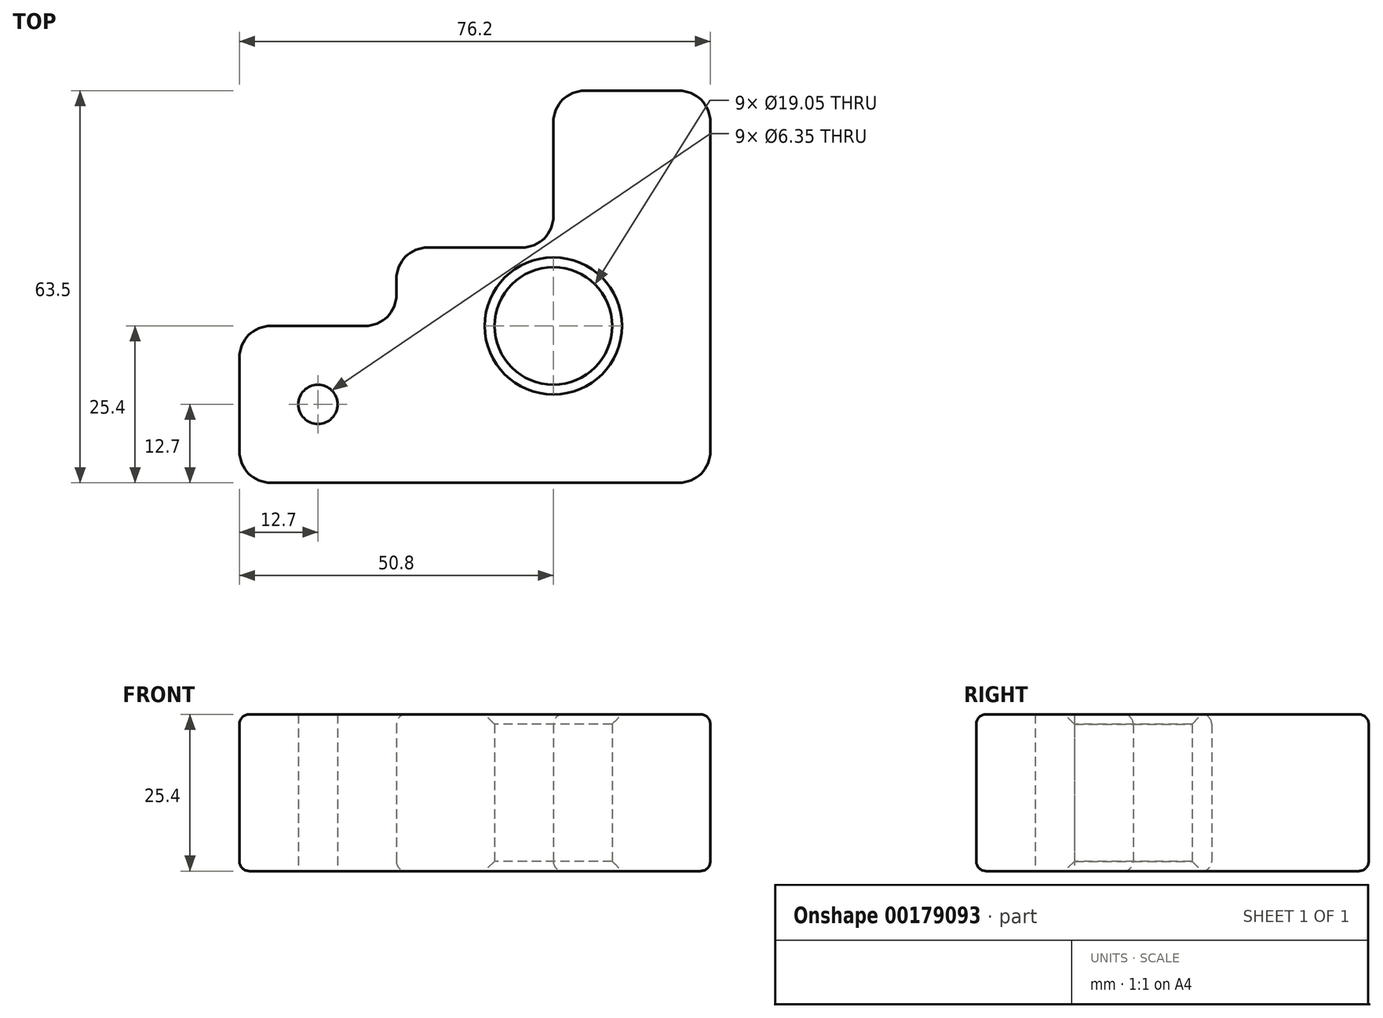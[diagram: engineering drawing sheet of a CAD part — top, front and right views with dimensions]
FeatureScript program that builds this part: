
annotation { "Feature Type Name" : "Feature", "Feature Type Description" : "" }
export const myFeature = defineFeature(function(context is Context, id is Id, definition is map)
    precondition{}
    {
        {
            var Q0;
            Q0=qCreatedBy(makeId("Top.planeOp"),FACE);
            var sketch = newSketch(context, id + "F0", { "sketchPlane" : qUnion([Q0])});
            skLineSegment(sketch, "E0", {"start": v(-25.4, 0) * mm, "end": v(0, 0) * mm});
            skLineSegment(sketch, "E1", {"start": v(0, 0) * mm, "end": v(0, 12.7) * mm});
            skLineSegment(sketch, "E2", {"start": v(0, 12.7) * mm, "end": v(25.4, 12.7) * mm});
            skLineSegment(sketch, "E3", {"start": v(25.4, 12.7) * mm, "end": v(25.4, 38.1) * mm});
            skLineSegment(sketch, "E4", {"start": v(25.4, 38.1) * mm, "end": v(50.8, 38.1) * mm});
            skLineSegment(sketch, "E5", {"start": v(50.8, 38.1) * mm, "end": v(50.8, -25.4) * mm});
            skLineSegment(sketch, "E6", {"start": v(50.8, -25.4) * mm, "end": v(-25.4, -25.4) * mm});
            skLineSegment(sketch, "E7", {"start": v(-25.4, -25.4) * mm, "end": v(-25.4, 0) * mm});
            skPoint(sketch, "E8", {"position": v(0, 0) * mm});
            skCircle(sketch, "E9", {"center": v(25.4, 0) * mm, "radius": 9.53 * mm});
            skCircle(sketch, "E10", {"center": v(-12.7, -12.7) * mm, "radius": 3.18 * mm});
            skSolve(sketch);
        }
        {
            var Q0;
            Q0=makeQuery(id+"F0.imprint","IMPRINT",FACE,{"disambiguationData":[TD([[makeQuery(id+"F0.imprint","IMPRINT",EDGE,{"derivedFrom":sQuery(id+"F0.wireOp",EDGE,"E0")}),-1.0]])]});
            extrude(context, id + "F1", {"entities" : qUnion([Q0]), "depth" : 25.4 * mm});
        }
        {
            var Q0;
            Q0=makeQuery(id+"F1.opExtrude","SWEPT_EDGE",EDGE,{"disambiguationData":[OSD([sQuery(id+"F0.wireOp",EDGE,"E4"),sQuery(id+"F0.wireOp",EDGE,"E5")])]});
            var Q1;
            Q1=makeQuery(id+"F1.opExtrude","SWEPT_EDGE",EDGE,{"disambiguationData":[OSD([sQuery(id+"F0.wireOp",EDGE,"E3"),sQuery(id+"F0.wireOp",EDGE,"E4")])]});
            var Q2;
            Q2=makeQuery(id+"F1.opExtrude","SWEPT_EDGE",EDGE,{"disambiguationData":[OSD([sQuery(id+"F0.wireOp",EDGE,"E2"),sQuery(id+"F0.wireOp",EDGE,"E3")])]});
            var Q3;
            Q3=makeQuery(id+"F1.opExtrude","SWEPT_EDGE",EDGE,{"disambiguationData":[OSD([sQuery(id+"F0.wireOp",EDGE,"E1"),sQuery(id+"F0.wireOp",EDGE,"E2")])]});
            var Q4;
            Q4=makeQuery(id+"F1.opExtrude","SWEPT_EDGE",EDGE,{"disambiguationData":[OSD([sQuery(id+"F0.wireOp",EDGE,"E0"),sQuery(id+"F0.wireOp",EDGE,"E1")])]});
            var Q5;
            Q5=makeQuery(id+"F1.opExtrude","SWEPT_EDGE",EDGE,{"disambiguationData":[OSD([sQuery(id+"F0.wireOp",EDGE,"E0"),sQuery(id+"F0.wireOp",EDGE,"E7")])]});
            var Q6;
            Q6=makeQuery(id+"F1.opExtrude","SWEPT_EDGE",EDGE,{"disambiguationData":[OSD([sQuery(id+"F0.wireOp",EDGE,"E6"),sQuery(id+"F0.wireOp",EDGE,"E7")])]});
            var Q7;
            Q7=makeQuery(id+"F1.opExtrude","SWEPT_EDGE",EDGE,{"disambiguationData":[OSD([sQuery(id+"F0.wireOp",EDGE,"E5"),sQuery(id+"F0.wireOp",EDGE,"E6")])]});
            fillet(context, id + "F2", {"entities" : qUnion([Q0, Q1, Q2, Q3, Q4, Q5, Q6, Q7]), "radius" : 5.08 * mm, "tangentPropagation" : true, "allowEdgeOverflow" : false});
        }
        {
            var Q0;
            Q0=makeQuery(id+"F1.opExtrude","CAP_EDGE",EDGE,{"disambiguationData":[OSD([sQuery(id+"F0.wireOp",EDGE,"E9")])],"isStart":false});
            chamfer(context, id + "F3", {"entities" : qUnion([Q0]), "width" : 1.59 * mm, "tangentPropagation" : true});
        }
        {
            var Q0;
            Q0=makeQuery(id+"F1.opExtrude","CAP_EDGE",EDGE,{"disambiguationData":[OSD([sQuery(id+"F0.wireOp",EDGE,"E7")])],"isStart":false});
            var Q1;
            Q1=makeQuery(id+"F1.opExtrude","CAP_EDGE",EDGE,{"disambiguationData":[OSD([sQuery(id+"F0.wireOp",EDGE,"E6")])],"isStart":true});
            fillet(context, id + "F4", {"entities" : qUnion([Q0, Q1]), "radius" : 1.59 * mm, "tangentPropagation" : true, "allowEdgeOverflow" : false});
        }
        {
            var Q0;
            Q0=makeQuery(id+"F1.opExtrude","CAP_EDGE",EDGE,{"disambiguationData":[OSD([sQuery(id+"F0.wireOp",EDGE,"E9")])],"isStart":true});
            chamfer(context, id + "F5", {"entities" : qUnion([Q0]), "width" : 1.59 * mm, "tangentPropagation" : true});
        }
    });
